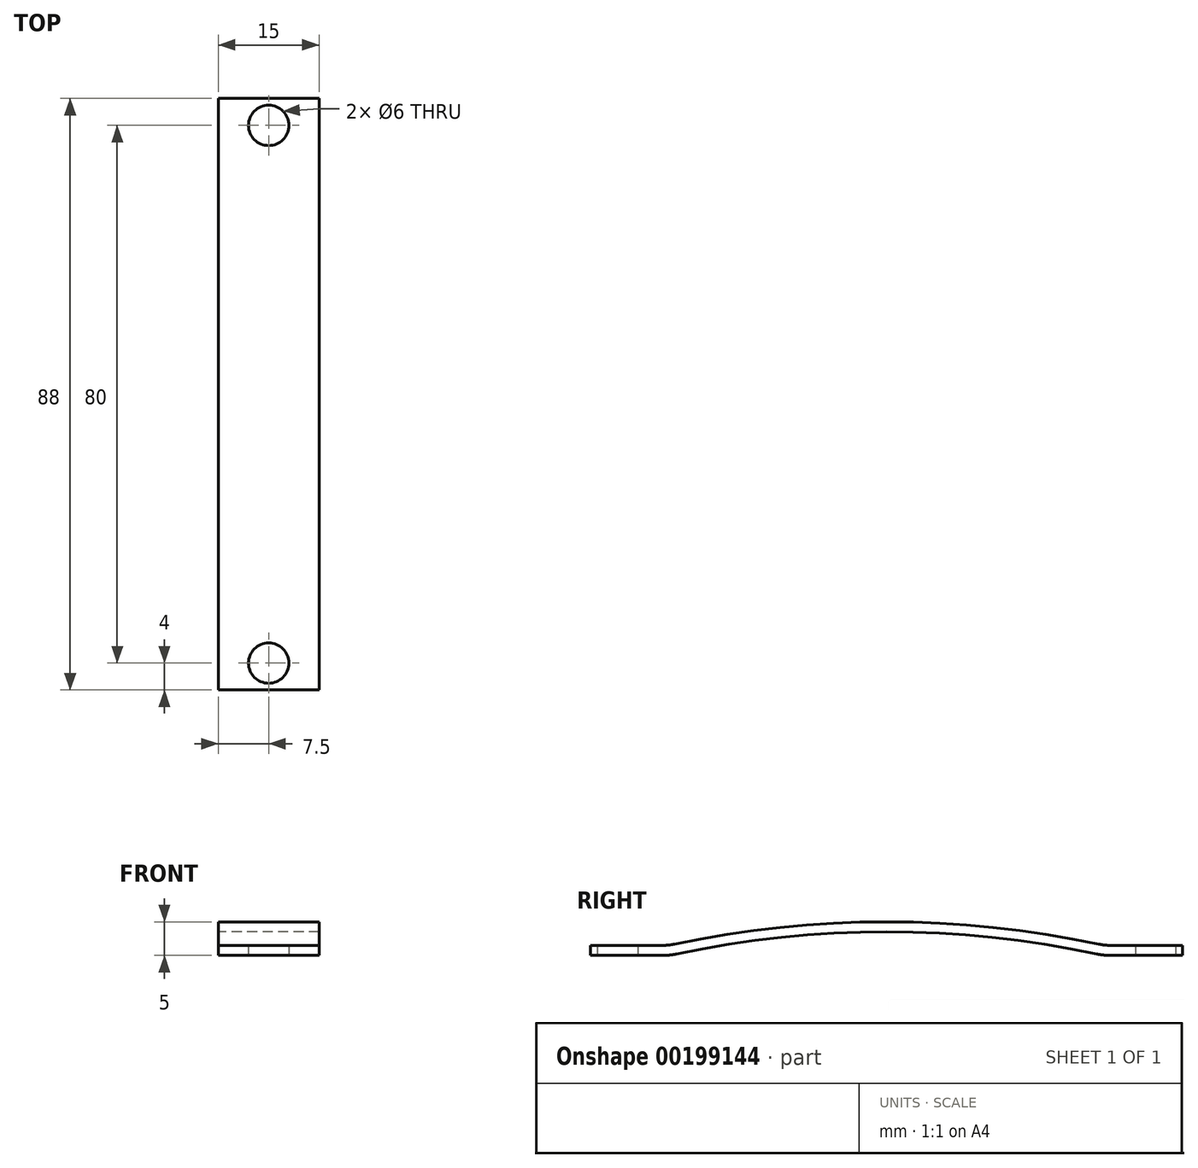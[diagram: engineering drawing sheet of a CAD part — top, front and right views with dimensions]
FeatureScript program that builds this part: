
annotation { "Feature Type Name" : "Feature", "Feature Type Description" : "" }
export const myFeature = defineFeature(function(context is Context, id is Id, definition is map)
    precondition{}
    {
        {
            var Q0;
            Q0=qCreatedBy(makeId("Right.planeOp"),FACE);
            var sketch = newSketch(context, id + "F0", { "sketchPlane" : qUnion([Q0])});
            skLineSegment(sketch, "E0", {"start": v(-44, 0) * mm, "end": v(-33.28, 0) * mm});
            skLineSegment(sketch, "E1", {"start": v(0, 0) * mm, "end": v(0, 3.5) * mm, "construction": true});
            skArc(sketch, "E2", {"start": v(0, 3.5) * mm, "mid": v(-15.69, 2.68) * mm, "end": v(-31.2, 0.22) * mm});
            skPoint(sketch, "E3.visualSharp", {"position": v(-32.21, 0) * mm});
            skArc(sketch, "E3.filletArc", {"start": v(-33.28, 0) * mm, "mid": v(-32.24, 0.05) * mm, "end": v(-31.2, 0.22) * mm});
            skArc(sketch, "E4.0", {"start": v(0, 5) * mm, "mid": v(-15.84, 4.17) * mm, "end": v(-31.51, 1.69) * mm});
            skArc(sketch, "E4.1", {"start": v(-33.28, 1.5) * mm, "mid": v(-32.4, 1.55) * mm, "end": v(-31.51, 1.69) * mm});
            skLineSegment(sketch, "E4.2", {"start": v(-44, 1.5) * mm, "end": v(-33.28, 1.5) * mm});
            skLineSegment(sketch, "E5", {"start": v(-44, 0) * mm, "end": v(-44, 1.5) * mm});
            skArc(sketch, "E6.MirrorCS", {"start": v(0, 5) * mm, "mid": v(15.84, 4.17) * mm, "end": v(31.51, 1.69) * mm});
            skArc(sketch, "E7.MirrorCS", {"start": v(33.28, 1.5) * mm, "mid": v(32.4, 1.55) * mm, "end": v(31.51, 1.69) * mm});
            skLineSegment(sketch, "E8.MirrorCS", {"start": v(44, 1.5) * mm, "end": v(33.28, 1.5) * mm});
            skLineSegment(sketch, "E9.MirrorCS", {"start": v(44, 0) * mm, "end": v(44, 1.5) * mm});
            skLineSegment(sketch, "E10.MirrorCS", {"start": v(44, 0) * mm, "end": v(33.28, 0) * mm});
            skArc(sketch, "E11.MirrorCS", {"start": v(33.28, 0) * mm, "mid": v(32.24, 0.05) * mm, "end": v(31.2, 0.22) * mm});
            skArc(sketch, "E12.MirrorCS", {"start": v(0, 3.5) * mm, "mid": v(15.69, 2.68) * mm, "end": v(31.2, 0.22) * mm});
            skSolve(sketch);
        }
        {
            var Q0;
            Q0 = qSketchRegion(id + "F0", true);
            extrude(context, id + "F1", {"entities" : qUnion([Q0]), "depth" : 7.5 * mm, "hasSecondDirection" : true, "secondDirectionOppositeDirection" : true, "secondDirectionDepth" : 7.5 * mm});
        }
        {
            var Q0;
            Q0=qCreatedBy(makeId("Top.planeOp"),FACE);
            var sketch = newSketch(context, id + "F2", { "sketchPlane" : qUnion([Q0])});
            skLineSegment(sketch, "E13", {"start": v(0, 0) * mm, "end": v(0, 40) * mm, "construction": true});
            skLineSegment(sketch, "E14", {"start": v(0, 0) * mm, "end": v(-2.97, 0) * mm, "construction": true});
            skCircle(sketch, "E15", {"center": v(0, 40) * mm, "radius": 3 * mm});
            skCircle(sketch, "E16.MirrorC", {"center": v(0, -40) * mm, "radius": 3 * mm});
            skSolve(sketch);
        }
        {
            var Q0;
            Q0 = qSketchRegion(id + "F2", true);
            extrude(context, id + "F3", {"entities" : qUnion([Q0]), "operationType" : NewBodyOperationType.REMOVE, "endBound" : BoundingType.THROUGH_ALL, "depth" : 25 * mm});
        }
    });
